# Revit family: PRD_FrankeWS_WshbsnTps_Plug-inPowerSupplyUnit_ACEX9002
name_source: partatom
category: Electrical Fixtures
revit_build: Autodesk Revit 2018 (Build: 20190510_1515(x64)
units: mm (PartAtom-declared; Revit-internal decimal feet)

## family parameters
Always vertical = No
Cut with Voids When Loaded = No
Maintain Annotation Orientation = No
OmniClass Number = 23.80.50.14
OmniClass Title = Plug Connectors
Part Type = Normal
Room Calculation Point = No
Round Connector Dimension = Use Diameter
Shared = No
Work Plane-Based = No

## types (1)
- ACEX9002
    AssetType = Fixed
    BIMObjectName = PRD_AR_WashbasinTaps_Plug-inPowerSupplyUnit_ACEX9002
    Category = Pr_40_20_87_98, Washbasin taps
    Communication = No
    CompatibleA3000 = No
    Description = Plug-in power supply with EU male connector, 100-240 V AC - 6.75 V DC.
    DurationUnit = year
    Features = EU male connector
    GrossWeight = 0.09 kg
    HasProtectiveEarth = 0
    IfcExportAs = IfcDistributionElement
    IfcExportType = USERDEFINED
    Manufacturer = KWC Group AG
    ManufacturerName = KWC Group AG
    ManufacturerURL = www.kwc.com
    Model = ACEX9002
    ModelNumber = 2030039823
    ModelReference = ACEX9002
    NBSDescription = Taps and water supply fittings for washbasins and troughs
    NBSReference = 45-35-70/371
    Name = Plug-in power supply unit ACEX9002
    NetWeight = 0.08 kg
    NominalDepth = 0 mm  [stored 0 ft]
    NominalFrequencyRange = 0 Hz
    NominalHeight = 63 mm  [stored 0.206693 ft]
    NominalWidth = 48 mm  [stored 0.15748 ft]
    NumberOfPoles = 0
    OutputVoltage = 6.75 Volt
    OutputVoltageUom = DC
    PowerFactor = 1
    PowerSwitch = No
    ProductCode = 230.0582.366
    ProductInformation = https://pim.kwc.com
    RatedCurrent = 0 A
    RatedVoltage = 240 V
    URL = www.kwc.com
    Uniclass2015Code = Pr_40_20_87_98
    Uniclass2015Title = Washbasin taps
    Uniclass2015Version = Products v1.23
    Version = 1
    WarrantyDurationUnit = year

note: [stored X ft] marks values corroborated as IEEE doubles in the binary element streams (Revit-internal decimal feet)

## geometry (parser evidence)
native form markers: Sweep x3
no freeform markers — native parametric forms only
